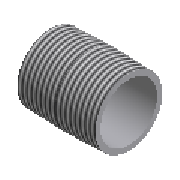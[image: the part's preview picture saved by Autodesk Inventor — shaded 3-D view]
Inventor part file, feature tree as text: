
AUTODESK INVENTOR PART (.ipt)
format: ipt  version: 2023.1 (Build 271208000, 208)  size: 160,256 bytes
history: native  units: mm (DEFAULTED — no unit token found)
features: other x6, revolve x1, sketch x1
ambient origin geometry x8: Origin, YZ Plane, XZ Plane, XY Plane, X Axis, Y Axis, Z Axis, Center Point
bodies: Solid1 (feature_tree)
feature tree (8):
  revolve  "Revolution1"  Angle=90.0deg
  other  "Work Point1"
  other  "Work Axis1"
  other  "Work Point2"
  other  "Work Axis2"
  other  "Work Point3"
  other  "Work Point4"
  sketch  "Sketch1"  dims[d0=52.9mm d12=90.0deg d1=0.312398mm d2=51.0mm d3=0.0mm d4=0.0mm d5=0.0mm d6=0.0mm d7=15.88mm d8=59.614mm]
